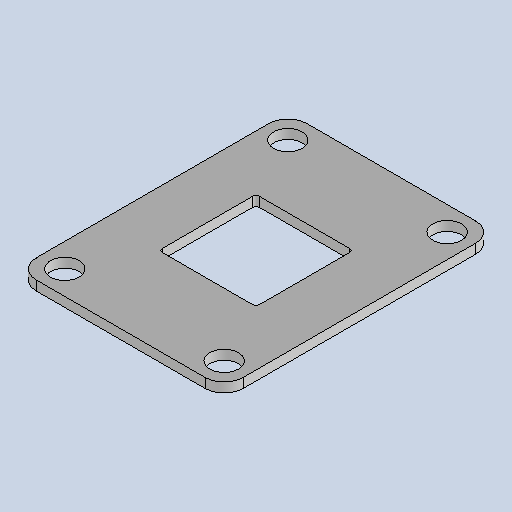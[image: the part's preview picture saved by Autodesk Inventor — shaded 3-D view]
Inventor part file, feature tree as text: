
AUTODESK INVENTOR PART (.ipt)
format: ipt  version: 2025.1 (Build 291241020, 241B)  size: 191,488 bytes
history: native  units: mm
features: other x3, chamfer x2, sketch x2, sheet_metal_op x1
ambient origin geometry x8: Origin, YZ Plane, XZ Plane, XY Plane, X Axis, Y Axis, Z Axis, Center Point
bodies: Body1 (feature_tree)
feature tree (8):
  sheet_metal_op  "Face3"
  chamfer  "Corner Round1"
  chamfer  "Corner Round2"
  sketch  "Sketch1"  dims[d154=65.0mm]
  other  "Plate5"
  sketch  "Sketch9"  dims[d155=85.0mm d156=3.0mm d172=30.5mm d173=70.0mm d174=9.0mm d175=50.0mm d176=3.0mm d177=0.0mm d178=6.0mm d179=1.0mm]
  other  "Cut2"
  other  "Definition1"
